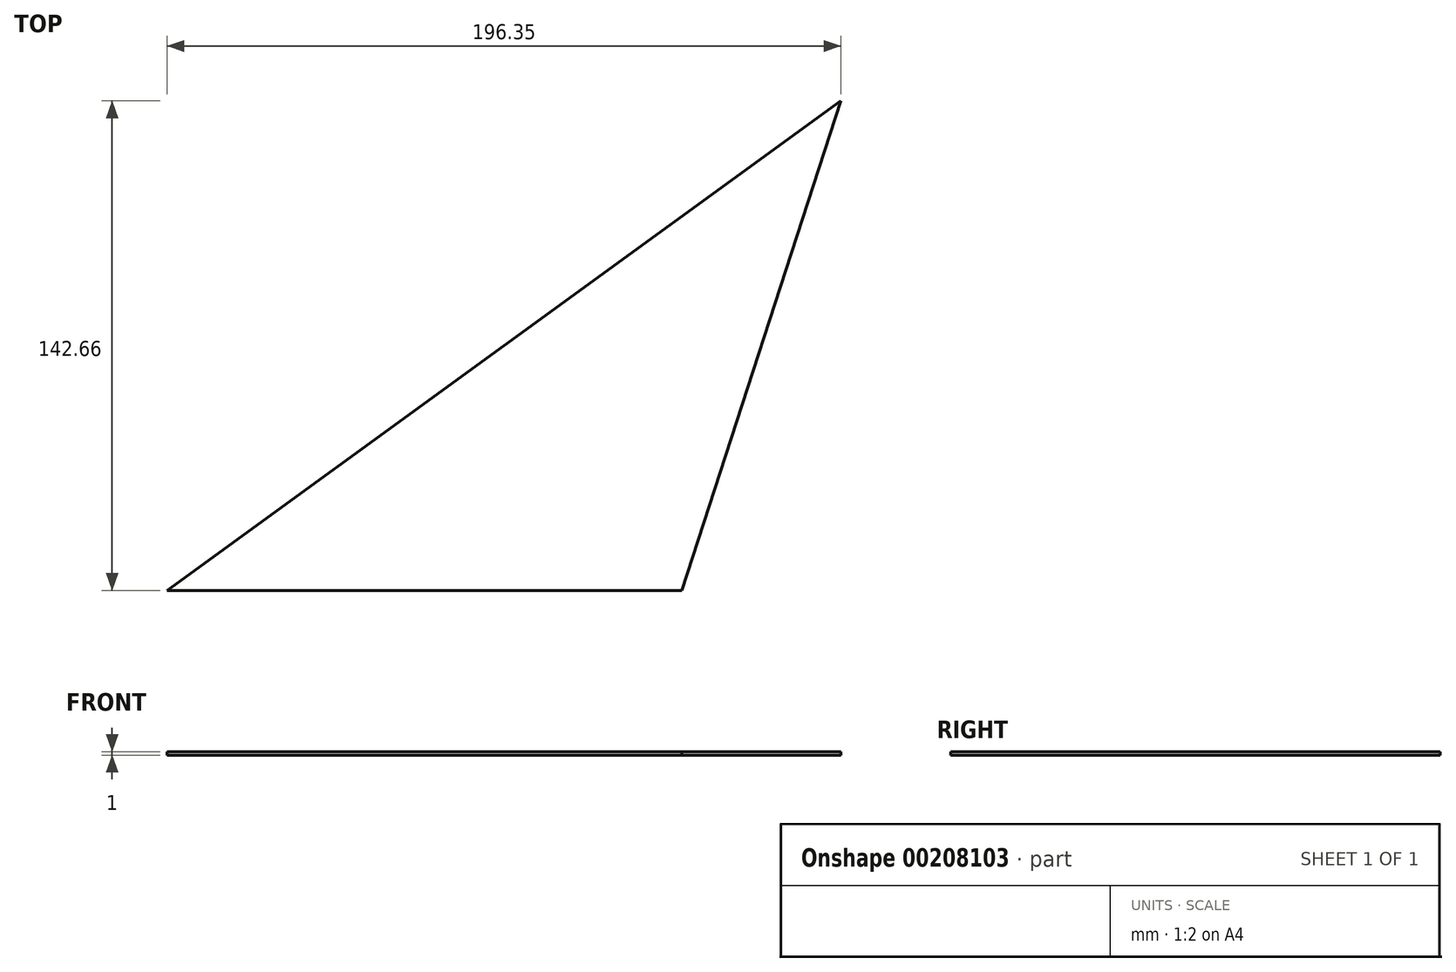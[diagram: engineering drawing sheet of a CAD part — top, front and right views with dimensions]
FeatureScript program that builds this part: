
annotation { "Feature Type Name" : "Feature", "Feature Type Description" : "" }
export const myFeature = defineFeature(function(context is Context, id is Id, definition is map)
    precondition{}
    {
        {
            var Q0;
            Q0=qCreatedBy(makeId("Top.planeOp"),FACE);
            var sketch = newSketch(context, id + "F0", { "sketchPlane" : qUnion([Q0])});
            skLineSegment(sketch, "E0", {"start": v(0, 0) * mm, "end": v(-150, 0) * mm});
            skLineSegment(sketch, "E1", {"start": v(-150, 0) * mm, "end": v(46.35, 142.66) * mm});
            skLineSegment(sketch, "E2", {"start": v(46.35, 142.66) * mm, "end": v(0, 0) * mm});
            skSolve(sketch);
        }
        {
            var Q0;
            Q0=makeQuery(id+"F0.imprint","IMPRINT",FACE,{"disambiguationData":[TD([[makeQuery(id+"F0.imprint","IMPRINT",EDGE,{"derivedFrom":sQuery(id+"F0.wireOp",EDGE,"E0")}),-1.0]])]});
            extrude(context, id + "F1", {"entities" : qUnion([Q0]), "depth" : 1 * mm});
        }
    });
